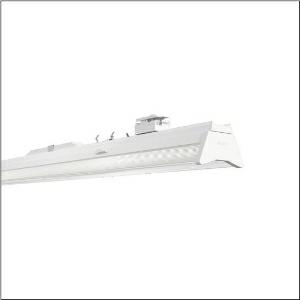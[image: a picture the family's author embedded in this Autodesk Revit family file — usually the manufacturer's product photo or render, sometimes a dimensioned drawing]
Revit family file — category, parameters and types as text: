
# Revit family: licross_r__11_performance_mo_51tm16dn4axg_9905
name_source: partatom
category: Lighting Fixtures
units: mm (PartAtom-declared; Revit-internal decimal feet)

## family parameters
Cut with Voids When Loaded = No
Host = Face
Light Source = No
Part Type = Normal
Room Calculation Point = No
Round Connector Dimension = Use Diameter
Shared = No

## types (1)
- --- (1 x LED, 10110 lm, 57.1 W, 4000K)
    Apparent Load = 57 VA
    CIE Flux Codes = 66 88 96 79 100
    Color Rendering = 80
    Color Temperature = 4000K
    Default Elevation = 1800 mm
    Description = Licross® 11 Performance MO, luminaire insert, of sheet steel, galvanised, coil coated, white, length: 1.500mm, width: 120mm, height: 123mm, LED rated luminous flux: 10.110lm, light colour: 840, control gear: DALI 2, with plug, 5-pole, with phase selection, mains connection: 220..240V, AC, 50/60Hz, rated input power: 57W, halogen-free wiring, primary light control with lens, of plastic, primary optical cover: cover, of PMMA, light emission: direct/indirect distribution, primary light characteristic: symmetric, protection rating (complete): IP40, insulation class (complete): insulation class I (protective earthing), certification: CE, ENEC, VDE, UKCA, protection symbol: D if used in an environment without relevant dust loads with corresponding accessories, impact resistance: IK06, permissible ambient temperature for indoor applications: -25..+35°C, corresponds to IFS (International Featured Standards) requirements for safety and quality in the food industry, reducing of maximum allowable ambient temperature of 5°C with ceiling mounting, LABS conformity tested according to VDMA 24364:2018-05, packaging unit: 1 piece
    Height = 114 mm
    Lamp = 1 x LED
    Lamp Light Flux = 10110 lm
    Lamp Power = 57.1 W
    Lamp count = 1
    Length = 1500 mm
    Luminous efficacy = 177 lm/W
    Manufacturer = Siteco
    ModVariant = No
    Model = 51TM16DN4AXG
    Mounting Place = Ceiling
    Mounting Type = Pendant
    Number of Poles = 1
    OnlyDefault = Yes
    Power Factor = 1
    Product Name = Licross® 11 Performance MO
    Product group = luminaire insert
    ProductGroupID = 902
    Protection Class = Protection class I
    Protection Degree = IP 40
    RLX_Detail_Level = 1
    RLX_Emergency_Light_Flux = 0 lm
    RLX_Emergency_Type = 0
    RLX_Emergency_Type_DB = No
    RlxData = <blob elided: 34105 chars, md5=465bfe10>
    Socket = socket
    Standby Power = 0 W
    System Light Flux = 10110 lm
    System Power = 57 W
    Type Comments = factory setting: luminous flux: 100 % | dim-lin: 254 | 378 mA
    Type Image = l_1256138.jpg
    URL = http://relux.com
    VarID = @adj_101350
    Voltage = 0 V
    Weight = 0.00 kg
    Width = 120 mm

## geometry (parser evidence)
native form markers: Blend x4, Sweep x13
no freeform markers — native parametric forms only
